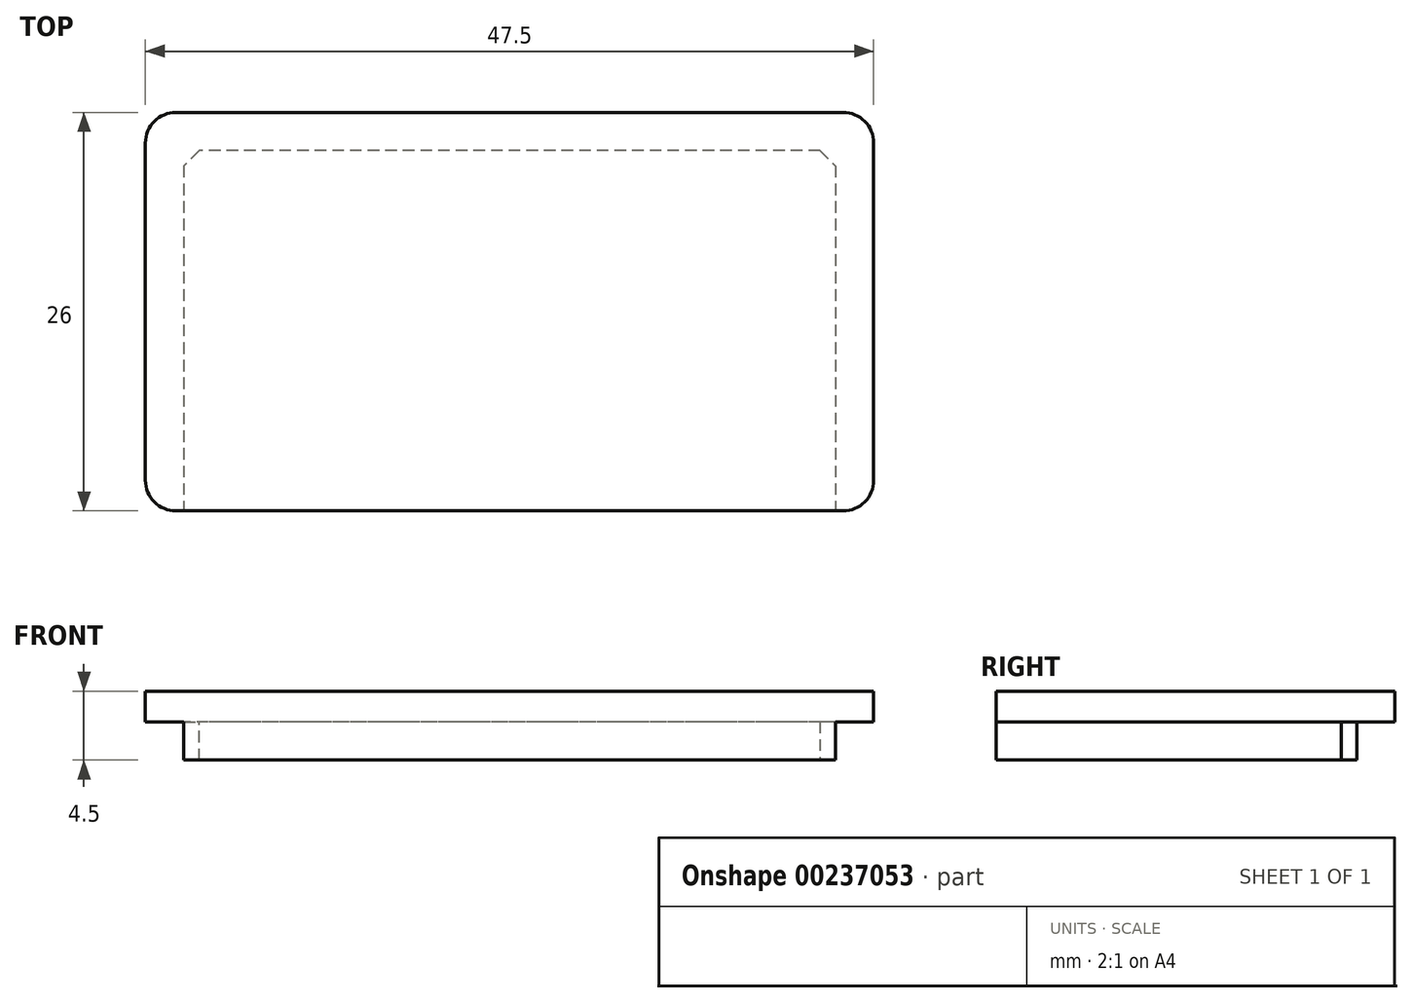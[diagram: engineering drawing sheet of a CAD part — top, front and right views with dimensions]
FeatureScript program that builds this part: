
annotation { "Feature Type Name" : "Feature", "Feature Type Description" : "" }
export const myFeature = defineFeature(function(context is Context, id is Id, definition is map)
    precondition{}
    {
        {
            var Q0;
            Q0=qCreatedBy(makeId("Top.planeOp"),FACE);
            var sketch = newSketch(context, id + "F0", { "sketchPlane" : qUnion([Q0])});
            skLineSegment(sketch, "E0.bottom", {"start": v(21.25, 11.75) * mm, "end": v(-21.25, 11.75) * mm});
            skLineSegment(sketch, "E0.top", {"start": v(21.25, -11.75) * mm, "end": v(-21.25, -11.75) * mm});
            skLineSegment(sketch, "E0.left", {"start": v(21.25, 11.75) * mm, "end": v(21.25, -11.75) * mm});
            skLineSegment(sketch, "E0.right", {"start": v(-21.25, 11.75) * mm, "end": v(-21.25, -11.75) * mm});
            skPoint(sketch, "E0.middle", {"position": v(0, 0) * mm});
            skSolve(sketch);
        }
        {
            var Q0;
            Q0=makeQuery(id+"F0.imprint","IMPRINT",FACE,{"disambiguationData":[TD([[makeQuery(id+"F0.imprint","IMPRINT",EDGE,{"derivedFrom":sQuery(id+"F0.wireOp",EDGE,"E0.bottom")}),1.0]])]});
            extrude(context, id + "F1", {"entities" : qUnion([Q0]), "depth" : 2.5 * mm});
        }
        {
            var Q0;
            Q0=makeQuery(id+"F1.opExtrude","CAP_FACE",FACE,{"disambiguationData":[OSD([sQuery(id+"F0.wireOp",EDGE,"E0.bottom"),sQuery(id+"F0.wireOp",EDGE,"E0.top"),sQuery(id+"F0.wireOp",EDGE,"E0.left"),sQuery(id+"F0.wireOp",EDGE,"E0.right")])],"isStart":false});
            var sketch = newSketch(context, id + "F2", { "sketchPlane" : qUnion([Q0])});
            skLineSegment(sketch, "E1.bottom", {"start": v(-23.75, -11.75) * mm, "end": v(23.75, -11.75) * mm});
            skLineSegment(sketch, "E1.top", {"start": v(-23.75, -11.75) * mm, "end": v(23.75, -11.75) * mm});
            skLineSegment(sketch, "E1.left", {"start": v(-23.75, -11.75) * mm, "end": v(-23.75, -11.75) * mm});
            skLineSegment(sketch, "E1.right", {"start": v(23.75, -11.75) * mm, "end": v(23.75, -11.75) * mm});
            skLineSegment(sketch, "E2", {"start": v(23.75, -11.75) * mm, "end": v(23.75, 14.25) * mm});
            skLineSegment(sketch, "E3", {"start": v(23.75, 14.25) * mm, "end": v(-23.75, 14.25) * mm});
            skLineSegment(sketch, "E4", {"start": v(-23.75, 14.25) * mm, "end": v(-23.75, -11.75) * mm});
            skSolve(sketch);
        }
        {
            var Q0;
            {var subQ0=sQuery(id+"F2.wireOp",EDGE,"E2");Q0=makeQuery(id+"F2.imprint","IMPRINT",FACE,{"disambiguationData":[TD([[makeQuery(id+"F2.imprint","IMPRINT",EDGE,{"derivedFrom":subQ0}),1.0]])]});}
            var Q1;
            Q1=makeQuery(id+"F2.imprint","IMPRINT",FACE,{"disambiguationData":[TD([[makeQuery(id+"F2.imprint","IMPRINT",EDGE,{"derivedFrom":makeQuery(id+"F1.opExtrude","CAP_EDGE",EDGE,{"disambiguationData":[OSD([sQuery(id+"F0.wireOp",EDGE,"E0.bottom")])],"isStart":false})}),1.0]])]});
            var Q2;
            Q2=makeQuery(id+"F0.imprint","IMPRINT",FACE,{"disambiguationData":[TD([[makeQuery(id+"F0.imprint","IMPRINT",EDGE,{"derivedFrom":sQuery(id+"F0.wireOp",EDGE,"E0.bottom")}),1.0]])]});
            extrude(context, id + "F3", {"entities" : qUnion([Q0, Q1, Q2]), "operationType" : NewBodyOperationType.ADD, "depth" : 2 * mm});
        }
        {
            var Q0;
            Q0=makeQuery(id+"F1.opExtrude","SWEPT_EDGE",EDGE,{"disambiguationData":[OSD([sQuery(id+"F0.wireOp",EDGE,"E0.bottom"),sQuery(id+"F0.wireOp",EDGE,"E0.left")])]});
            var Q1;
            Q1=makeQuery(id+"F1.opExtrude","SWEPT_EDGE",EDGE,{"disambiguationData":[OSD([sQuery(id+"F0.wireOp",EDGE,"E0.bottom"),sQuery(id+"F0.wireOp",EDGE,"E0.right")])]});
            chamfer(context, id + "F4", {"entities" : qUnion([Q0, Q1]), "width" : 1 * mm, "tangentPropagation" : true});
        }
        {
            var Q0;
            Q0=makeQuery(id+"F3.opExtrude","SWEPT_EDGE",EDGE,{"disambiguationData":[OSD([sQuery(id+"F2.wireOp",EDGE,"E2"),sQuery(id+"F2.wireOp",EDGE,"E3")])]});
            var Q1;
            Q1=makeQuery(id+"F3.opExtrude","SWEPT_EDGE",EDGE,{"disambiguationData":[OSD([sQuery(id+"F2.wireOp",EDGE,"E1.top"),sQuery(id+"F2.wireOp",EDGE,"E2")])]});
            var Q2;
            Q2=makeQuery(id+"F3.opExtrude","SWEPT_EDGE",EDGE,{"disambiguationData":[OSD([sQuery(id+"F2.wireOp",EDGE,"E3"),sQuery(id+"F2.wireOp",EDGE,"E4")])]});
            var Q3;
            Q3=makeQuery(id+"F3.opExtrude","SWEPT_EDGE",EDGE,{"disambiguationData":[OSD([sQuery(id+"F2.wireOp",EDGE,"E1.top"),sQuery(id+"F2.wireOp",EDGE,"E4")])]});
            fillet(context, id + "F5", {"entities" : qUnion([Q0, Q1, Q2, Q3]), "radius" : 2 * mm, "tangentPropagation" : true, "allowEdgeOverflow" : false});
        }
    });
